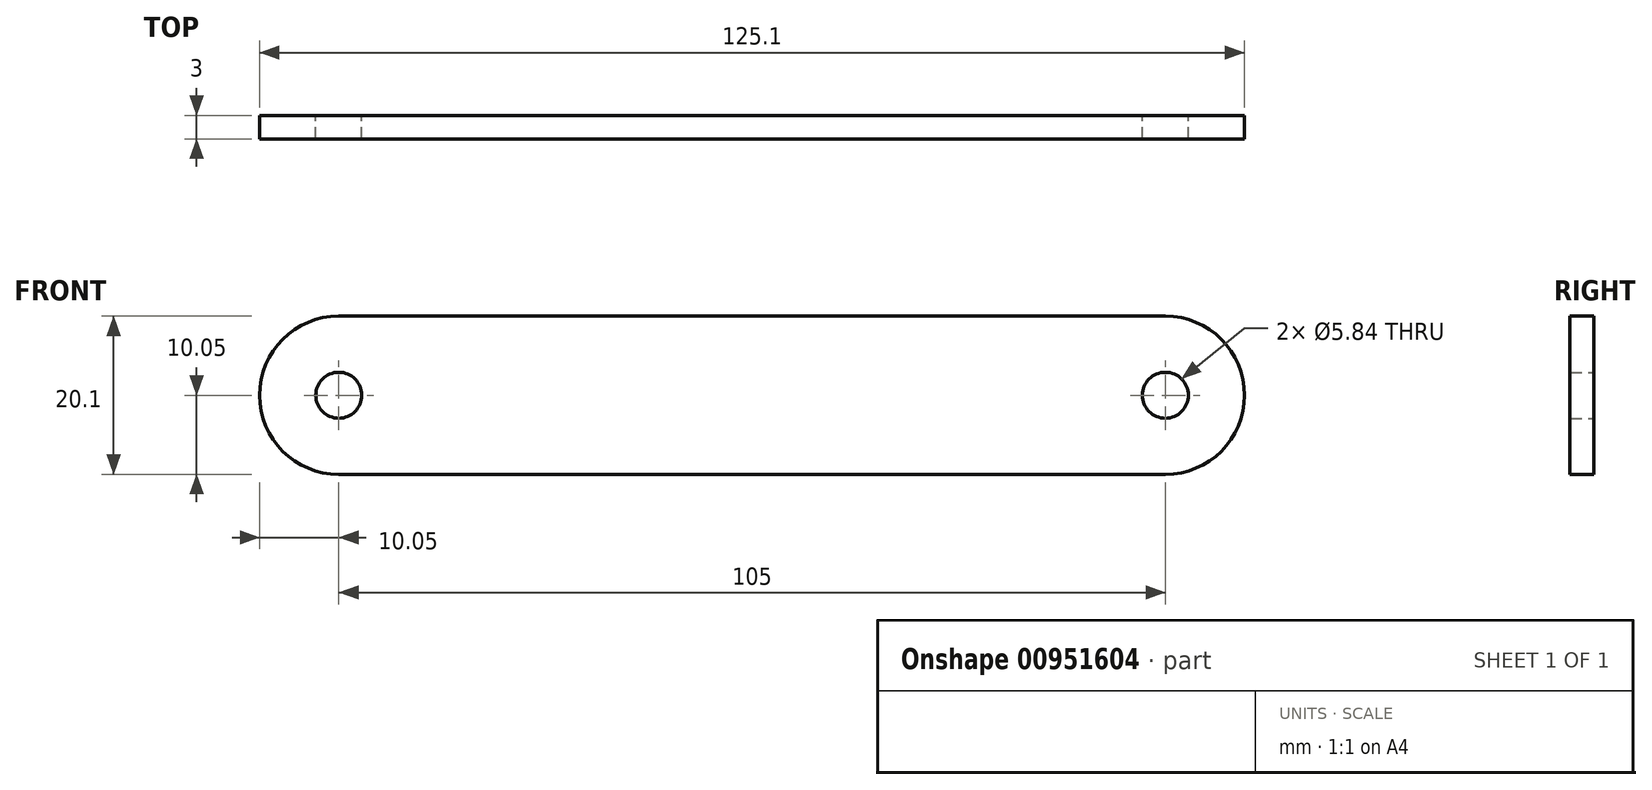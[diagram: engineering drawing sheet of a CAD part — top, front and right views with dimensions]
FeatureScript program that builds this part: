
annotation { "Feature Type Name" : "Feature", "Feature Type Description" : "" }
export const myFeature = defineFeature(function(context is Context, id is Id, definition is map)
    precondition{}
    {
        {
            var Q0;
            Q0=qCreatedBy(makeId("Front.planeOp"),FACE);
            var sketch = newSketch(context, id + "F0", { "sketchPlane" : qUnion([Q0])});
            skLineSegment(sketch, "E0.bottom", {"start": v(52.5, 10.05) * mm, "end": v(-52.5, 10.05) * mm});
            skLineSegment(sketch, "E0.top", {"start": v(52.5, -10.05) * mm, "end": v(-52.5, -10.05) * mm});
            skPoint(sketch, "E0.middle", {"position": v(0, 0) * mm});
            skArc(sketch, "E1", {"start": v(-52.5, 10.05) * mm, "mid": v(-62.55, 0) * mm, "end": v(-52.5, -10.05) * mm});
            skArc(sketch, "E2.MirrorCS", {"start": v(52.5, 10.05) * mm, "mid": v(62.55, 0) * mm, "end": v(52.5, -10.05) * mm});
            skCircle(sketch, "E3", {"center": v(-52.5, 0) * mm, "radius": 2.92 * mm});
            skCircle(sketch, "E4.MirrorC", {"center": v(52.5, 0) * mm, "radius": 2.92 * mm});
            skSolve(sketch);
        }
        {
            var Q0;
            Q0 = qSketchRegion(id + "F0", true);
            extrude(context, id + "F1", {"entities" : qUnion([Q0]), "depth" : 3 * mm, "offsetDistance" : 25 * mm});
        }
    });
